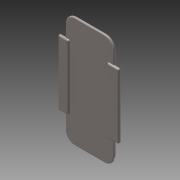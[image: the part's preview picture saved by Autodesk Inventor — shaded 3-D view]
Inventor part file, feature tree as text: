
AUTODESK INVENTOR PART (.ipt)
format: ipt  version: 2015 (Build 190159000, 159)  size: 218,112 bytes
history: native  units: mm
features: extrude x4, fillet x3, sketch x2, chamfer x1
ambient origin geometry x8: Origin, YZ Plane, XZ Plane, XY Plane, X Axis, Y Axis, Z Axis, Center Point
bodies: Solid1 (feature_tree)
feature tree (10):
  extrude  "Extrusion1"  Depth=5.0mm
  fillet  "Fillet1"  Radius=5.0mm
  extrude  "Extrusion3"  Depth=2.0mm
  extrude  "Extrusion4"  Depth=10.0mm
  extrude  "Extrusion5"  Depth=2.0mm
  chamfer  "Chamfer2"  Distance=3.0mm
  fillet  "Fillet3"  Radius=136.0mm
  fillet  "Fillet4"  Radius=6.0mm
  sketch  "Sketch3"  dims[d0=231.3mm d1=101.2mm d2=5.0mm d3=0.0mm]
  sketch  "Sketch4"  dims[d4=20.0mm d14=45.0mm d18=10.0mm d19=136.0mm d20=3.0mm d21=0.0mm d22=136.0mm d23=6.0mm d24=13.0mm d25=0.0mm d26=136.0mm d27=6.0mm d28=13.0mm d29=0.0mm d30=3.0mm d31=2.0mm d32=45.0deg d33=3.0mm d34=2.0mm]
